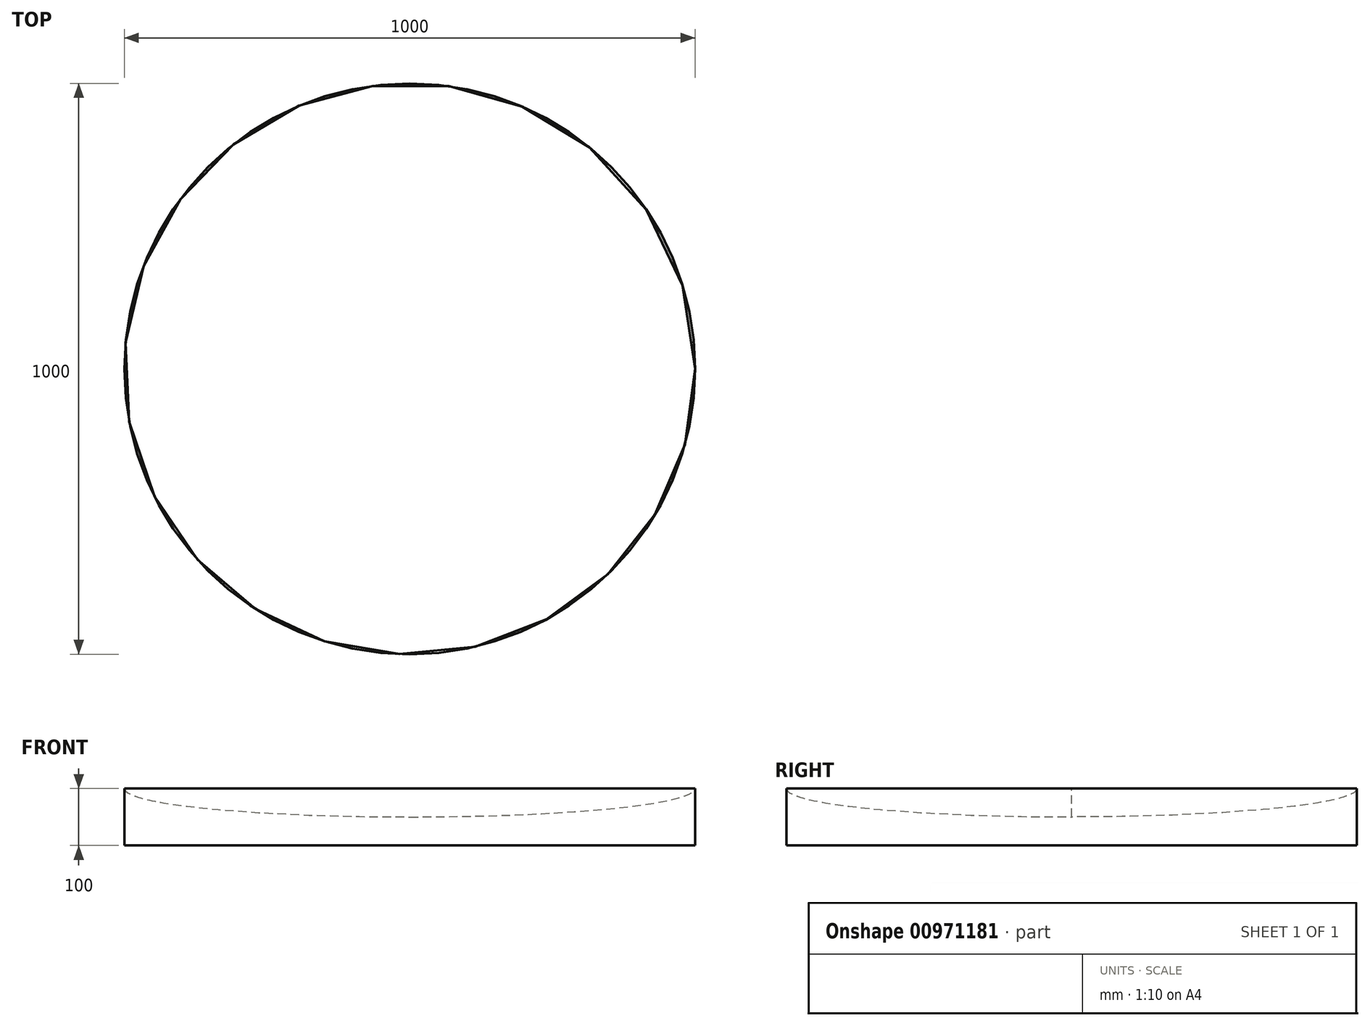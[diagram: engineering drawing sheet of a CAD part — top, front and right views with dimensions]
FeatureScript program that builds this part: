
annotation { "Feature Type Name" : "Feature", "Feature Type Description" : "" }
export const myFeature = defineFeature(function(context is Context, id is Id, definition is map)
    precondition{}
    {
        {
            var Q0;
            Q0=qCreatedBy(makeId("Top.planeOp"),FACE);
            var sketch = newSketch(context, id + "F0", { "sketchPlane" : qUnion([Q0])});
            skCircle(sketch, "E0", {"center": v(0, 0) * mm, "radius": 500 * mm});
            skSolve(sketch);
        }
        {
            var Q0;
            Q0=makeQuery(id+"F0.imprint","IMPRINT",FACE,{"disambiguationData":[TD([[makeQuery(id+"F0.imprint","IMPRINT",EDGE,{"derivedFrom":sQuery(id+"F0.wireOp",EDGE,"E0")}),1.0]])]});
            extrude(context, id + "F1", {"entities" : qUnion([Q0]), "depth" : 100 * mm, "offsetDistance" : 25 * mm});
        }
        {
            var Q0;
            Q0=qCreatedBy(makeId("Front.planeOp"),FACE);
            var sketch = newSketch(context, id + "F2", { "sketchPlane" : qUnion([Q0])});
            skEllipticalArc(sketch, "E1", {});
            skLineSegment(sketch, "E2", {"start": v(0, 50) * mm, "end": v(0, 0) * mm});
            skLineSegment(sketch, "E3", {"start": v(0, 0) * mm, "end": v(500, 0) * mm});
            skLineSegment(sketch, "E4", {"start": v(500, 0) * mm, "end": v(500, 100) * mm});
            const initialGuessF2  = {"E1": [0, 0.1, 1, 0, 0.5, 0.05, 4.71238898038469, 0]};
            skSetInitialGuess(sketch, initialGuessF2);
            skSolve(sketch);
        }
        {
            var Q0;
            Q0 = qSketchRegion(id + "F2", true);
            var Q1;
            Q1=sQuery(id+"F2.wireOp",EDGE,"E2");
            revolve(context, id + "F3", {"surfaceOperationType" : NewSurfaceOperationType.NEW, "entities" : qUnion([Q0]), "axis" : qUnion([Q1]), "revolveType" : RevolveType.FULL});
        }
    });
